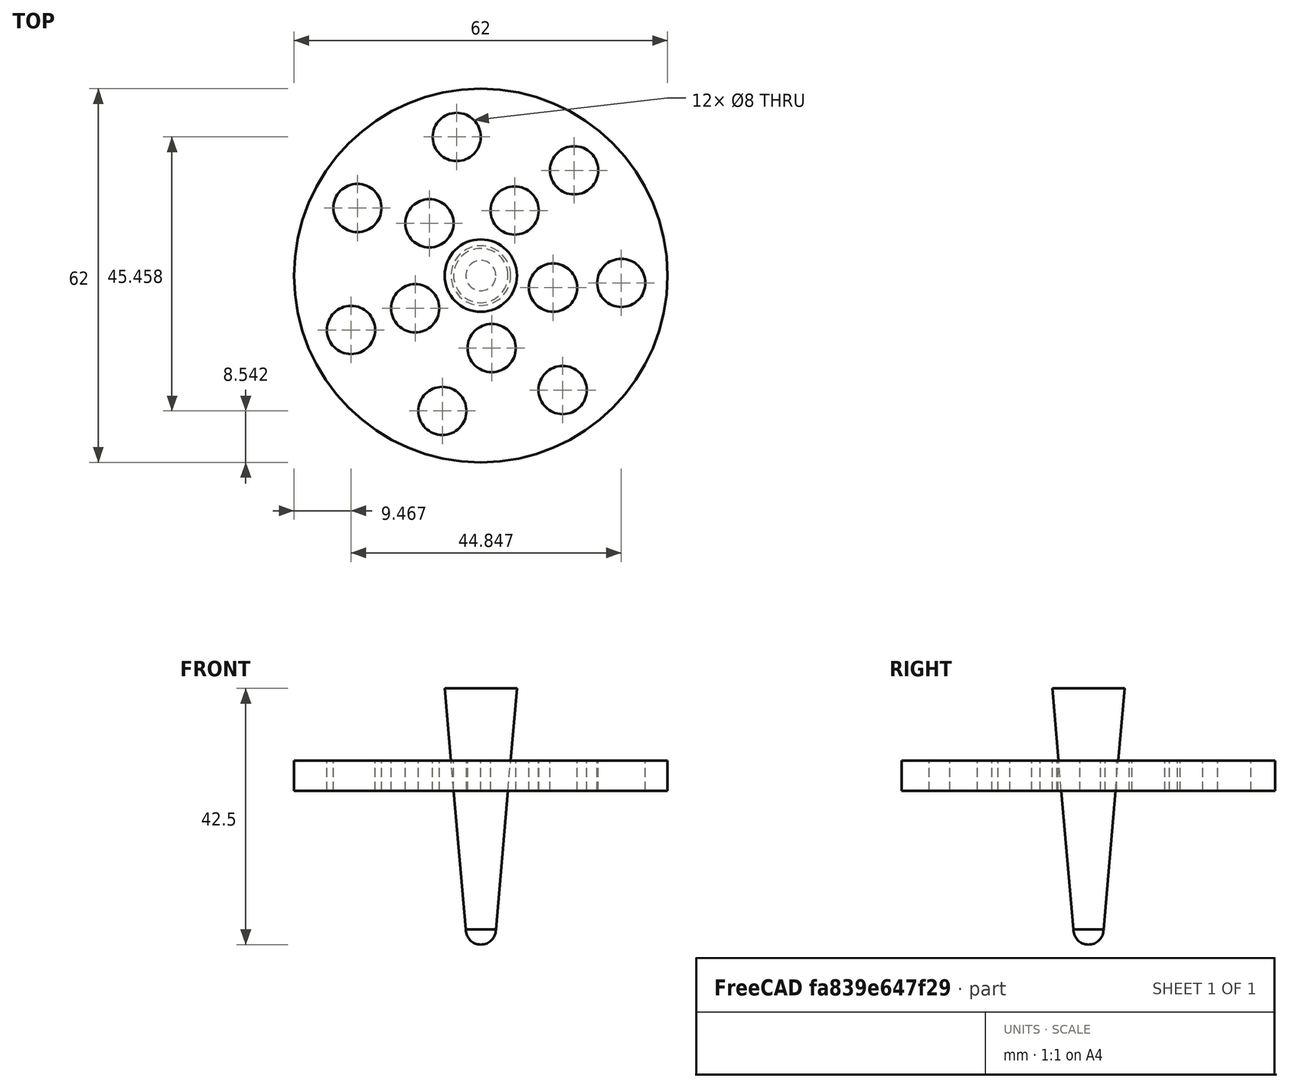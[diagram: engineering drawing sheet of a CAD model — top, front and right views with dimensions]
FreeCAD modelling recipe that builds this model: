
FCSTD DOCUMENT  (FreeCAD 0.16R6705 (Git))
Label: j-gyroscope-fusion-v1-BASE
License: All rights reserved
LicenseURL: http://en.wikipedia.org/wiki/All_rights_reserved
objects: Part::Cylinder×4, Part::Cut×4, Part::FeaturePython×2, Part::Cone×2, Part::Sphere×2, Part::Fuse×2
note: 16 computed .brp shape members not serialized (recipe doc carries the construction recipe); baked Part::Feature solids carry a one-line shape summary decoded from their .brp

FEATURE [Part::Cylinder] Cylinder  label="Base"
  Angle = 360
  Height = 5
  Radius = 31
FEATURE [Part::Cylinder] Cylinder001  label="Aguja central"
  Angle = 360
  Height = 20
  Placement = pos=(0,0,-7) rot=(0,0,1;0rad)
  Radius = 1
FEATURE [Part::Cylinder] Cylinder002  label="Cilindro plastilina"
  Angle = 360
  Height = 20
  Placement = pos=(12,-2,-7) rot=(0,0,1;0rad)
  Radius = 4
FEATURE [Part::FeaturePython] Array  # Draft array (typed FeaturePython)
  Angle = 360
  ArrayType = 1
  Axis = (0,0,1)
  Base = -> Cylinder002
  Center = (0,0,0)
  Fuse = false
  IntervalAxis = (0,0,0)
  IntervalX = (1,0,0)
  IntervalY = (0,1,0)
  IntervalZ = (0,0,0)
  NumberPolar = 5
  NumberX = 2
  NumberY = 2
  NumberZ = 1
FEATURE [Part::Cylinder] Cylinder003  label="Cilindro plastilina exterior"
  Angle = 360
  Height = 20
  Placement = pos=(-4,23,0) rot=(0,0,1;0rad)
  Radius = 4
FEATURE [Part::FeaturePython] Array001  label="Array Exterior"  # Draft array (typed FeaturePython)
  Angle = 360
  ArrayType = 1
  Axis = (0,0,1)
  Base = -> Cylinder003
  Center = (0,0,0)
  Fuse = false
  IntervalAxis = (0,0,0)
  IntervalX = (1,0,0)
  IntervalY = (0,1,0)
  IntervalZ = (0,0,0)
  NumberPolar = 7
  NumberX = 2
  NumberY = 2
  NumberZ = 1
  Placement = pos=(0,0,-7) rot=(0,0,1;0rad)
FEATURE [Part::Cut] Cut
  Base = -> Cylinder
  Tool = -> Array
FEATURE [Part::Cut] Cut001  label="base fusionada"
  Base = -> Cut
  Tool = -> Array001
FEATURE [Part::Cut] Cut002  label="Gyroscopio"
  Base = -> Cut001
  Tool = -> Cylinder001
FEATURE [Part::Cone] Cone  label="Aguja central solo"
  Angle = 360
  Height = 40
  Radius1 = 2.5
  Radius2 = 6
FEATURE [Part::Sphere] Sphere  label="Esfera"
  Angle1 = -90
  Angle2 = 90
  Angle3 = 360
  Radius = 2.5
FEATURE [Part::Fuse] Fusion  label="Aguja pieza"
  Base = -> Cone
  Placement = pos=(0,0,-23) rot=(0,0,1;0rad)
  Tool = -> Sphere
FEATURE [Part::Cut] Cut003
  Base = -> Cut002
  Tool = -> Fusion
FEATURE [Part::Cone] Cone001  label="Aguja central solo001"
  Angle = 360
  Height = 40
  Radius1 = 2.5
  Radius2 = 6
FEATURE [Part::Sphere] Sphere001  label="Esfera001"
  Angle1 = -90
  Angle2 = 90
  Angle3 = 360
  Radius = 2.5
FEATURE [Part::Fuse] Fusion001  label="Aguja pieza001"
  Base = -> Cone001
  Placement = pos=(0,0,-23) rot=(0,0,1;0rad)
  Tool = -> Sphere001
